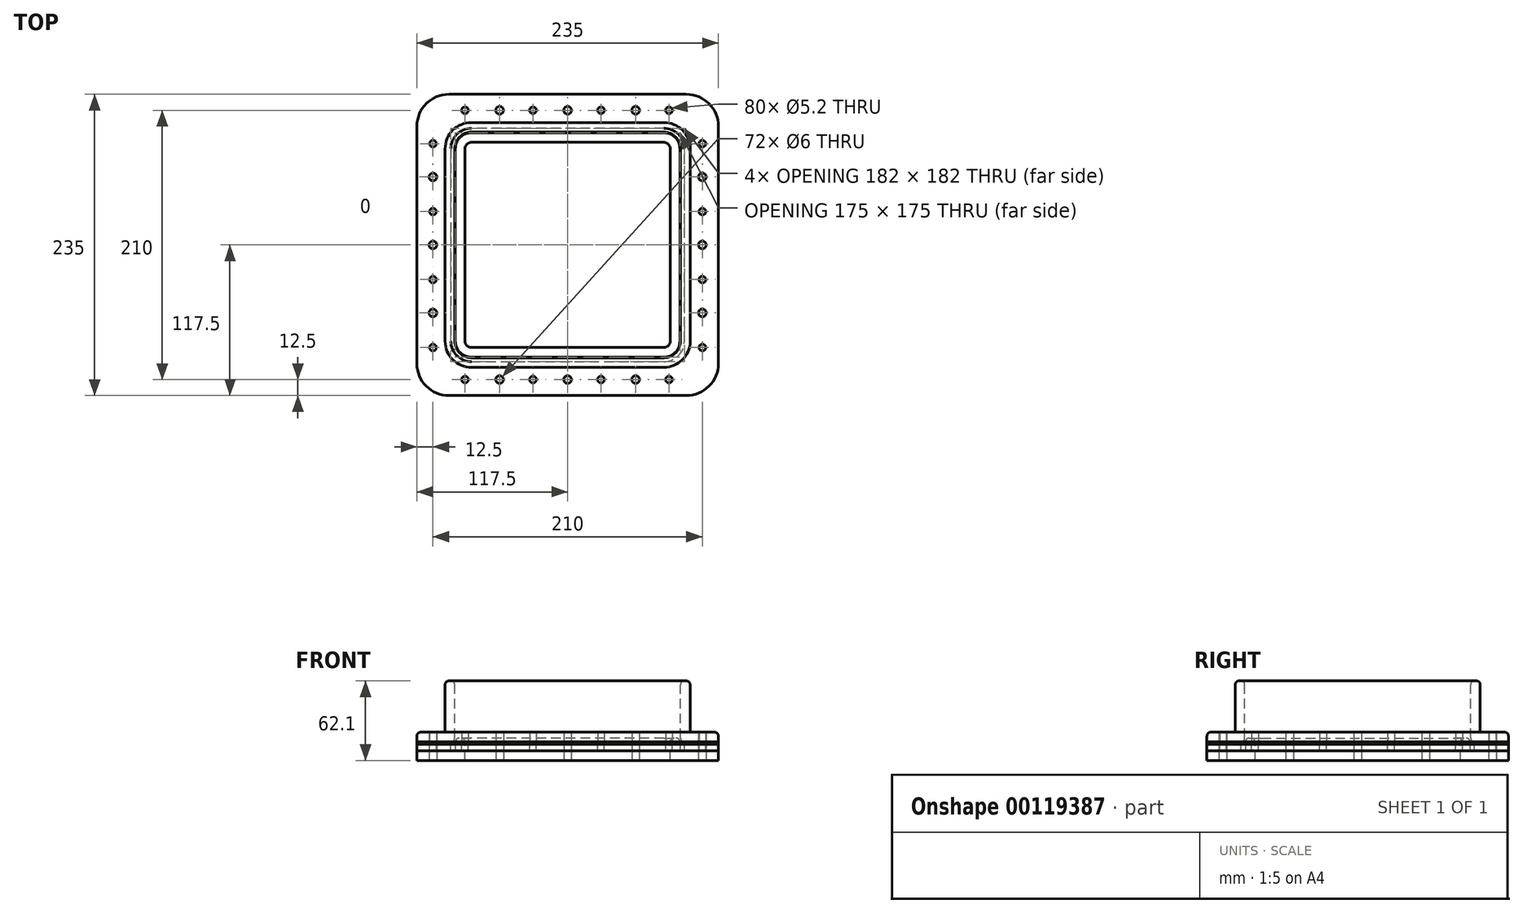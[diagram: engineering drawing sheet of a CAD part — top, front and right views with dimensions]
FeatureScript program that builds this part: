
annotation { "Feature Type Name" : "Feature", "Feature Type Description" : "" }
export const myFeature = defineFeature(function(context is Context, id is Id, definition is map)
    precondition{}
    {
        {
            var Q0;
            Q0=qCreatedBy(makeId("Top.planeOp"),FACE);
            var sketch = newSketch(context, id + "F0", { "sketchPlane" : qUnion([Q0])});
            skLineSegment(sketch, "E0.bottom", {"start": v(75, -80) * mm, "end": v(-75, -80) * mm});
            skLineSegment(sketch, "E0.top", {"start": v(75, 80) * mm, "end": v(-75, 80) * mm});
            skLineSegment(sketch, "E0.left", {"start": v(80, -75) * mm, "end": v(80, 75) * mm});
            skLineSegment(sketch, "E0.right", {"start": v(-80, -75) * mm, "end": v(-80, 75) * mm});
            skPoint(sketch, "E0.middle", {"position": v(0, 0) * mm});
            skLineSegment(sketch, "E1.bottom", {"start": v(75, -87.5) * mm, "end": v(-75, -87.5) * mm});
            skLineSegment(sketch, "E1.top", {"start": v(75, 87.5) * mm, "end": v(-75, 87.5) * mm});
            skLineSegment(sketch, "E1.left", {"start": v(87.5, -75) * mm, "end": v(87.5, 75) * mm});
            skLineSegment(sketch, "E1.right", {"start": v(-87.5, -75) * mm, "end": v(-87.5, 75) * mm});
            skLineSegment(sketch, "E2.bottom", {"start": v(92.5, -117.5) * mm, "end": v(-92.5, -117.5) * mm});
            skLineSegment(sketch, "E2.top", {"start": v(92.5, 117.5) * mm, "end": v(-92.5, 117.5) * mm});
            skLineSegment(sketch, "E2.left", {"start": v(117.5, -92.5) * mm, "end": v(117.5, 92.5) * mm});
            skLineSegment(sketch, "E2.right", {"start": v(-117.5, -92.5) * mm, "end": v(-117.5, 92.5) * mm});
            skPoint(sketch, "E3.visualSharp", {"position": v(-117.5, 117.5) * mm});
            skArc(sketch, "E3.filletArc", {"start": v(-92.5, 117.5) * mm, "mid": v(-110.18, 110.18) * mm, "end": v(-117.5, 92.5) * mm});
            skPoint(sketch, "E4.visualSharp", {"position": v(117.5, 117.5) * mm});
            skArc(sketch, "E4.filletArc", {"start": v(117.5, 92.5) * mm, "mid": v(110.18, 110.18) * mm, "end": v(92.5, 117.5) * mm});
            skPoint(sketch, "E5.visualSharp", {"position": v(117.5, -117.5) * mm});
            skArc(sketch, "E5.filletArc", {"start": v(92.5, -117.5) * mm, "mid": v(110.18, -110.18) * mm, "end": v(117.5, -92.5) * mm});
            skPoint(sketch, "E6.visualSharp", {"position": v(-117.5, -117.5) * mm});
            skArc(sketch, "E6.filletArc", {"start": v(-117.5, -92.5) * mm, "mid": v(-110.18, -110.18) * mm, "end": v(-92.5, -117.5) * mm});
            skPoint(sketch, "E7.visualSharp", {"position": v(-80, 80) * mm});
            skArc(sketch, "E7.filletArc", {"start": v(-75, 80) * mm, "mid": v(-78.54, 78.54) * mm, "end": v(-80, 75) * mm});
            skPoint(sketch, "E8.visualSharp", {"position": v(80, 80) * mm});
            skArc(sketch, "E8.filletArc", {"start": v(80, 75) * mm, "mid": v(78.54, 78.54) * mm, "end": v(75, 80) * mm});
            skPoint(sketch, "E9.visualSharp", {"position": v(80, -80) * mm});
            skArc(sketch, "E9.filletArc", {"start": v(75, -80) * mm, "mid": v(78.54, -78.54) * mm, "end": v(80, -75) * mm});
            skPoint(sketch, "E10.visualSharp", {"position": v(-80, -80) * mm});
            skArc(sketch, "E10.filletArc", {"start": v(-80, -75) * mm, "mid": v(-78.54, -78.54) * mm, "end": v(-75, -80) * mm});
            skPoint(sketch, "E11.visualSharp", {"position": v(-87.5, 87.5) * mm});
            skArc(sketch, "E11.filletArc", {"start": v(-75, 87.5) * mm, "mid": v(-83.84, 83.84) * mm, "end": v(-87.5, 75) * mm});
            skPoint(sketch, "E12.visualSharp", {"position": v(87.5, 87.5) * mm});
            skArc(sketch, "E12.filletArc", {"start": v(87.5, 75) * mm, "mid": v(83.84, 83.84) * mm, "end": v(75, 87.5) * mm});
            skPoint(sketch, "E13.visualSharp", {"position": v(87.5, -87.5) * mm});
            skArc(sketch, "E13.filletArc", {"start": v(75, -87.5) * mm, "mid": v(83.84, -83.84) * mm, "end": v(87.5, -75) * mm});
            skPoint(sketch, "E14.visualSharp", {"position": v(-87.5, -87.5) * mm});
            skArc(sketch, "E14.filletArc", {"start": v(-87.5, -75) * mm, "mid": v(-83.84, -83.84) * mm, "end": v(-75, -87.5) * mm});
            skSolve(sketch);
        }
        {
            var Q0;
            Q0=makeQuery(id+"F0.imprint","IMPRINT",FACE,{"disambiguationData":[TD([[makeQuery(id+"F0.imprint","IMPRINT",EDGE,{"derivedFrom":sQuery(id+"F0.wireOp",EDGE,"E0.bottom")}),1.0]])]});
            extrude(context, id + "F1", {"entities" : qUnion([Q0]), "depth" : 25 * mm});
        }
        {
            var Q0;
            Q0 = qSketchRegion(id + "F0", true);
            extrude(context, id + "F2", {"entities" : qUnion([Q0]), "operationType" : NewBodyOperationType.ADD, "depth" : 10 * mm});
        }
        {
            var Q0;
            Q0=makeQuery(id+"F1.opExtrude","CAP_FACE",FACE,{"disambiguationData":[OSD([sQuery(id+"F0.wireOp",EDGE,"E0.bottom"),sQuery(id+"F0.wireOp",EDGE,"E0.top"),sQuery(id+"F0.wireOp",EDGE,"E0.left"),sQuery(id+"F0.wireOp",EDGE,"E0.right"),sQuery(id+"F0.wireOp",EDGE,"E1.bottom"),sQuery(id+"F0.wireOp",EDGE,"E1.top"),sQuery(id+"F0.wireOp",EDGE,"E1.left"),sQuery(id+"F0.wireOp",EDGE,"E1.right"),sQuery(id+"F0.wireOp",EDGE,"E7.filletArc"),sQuery(id+"F0.wireOp",EDGE,"E8.filletArc"),sQuery(id+"F0.wireOp",EDGE,"E9.filletArc"),sQuery(id+"F0.wireOp",EDGE,"E10.filletArc"),sQuery(id+"F0.wireOp",EDGE,"E11.filletArc"),sQuery(id+"F0.wireOp",EDGE,"E12.filletArc"),sQuery(id+"F0.wireOp",EDGE,"E13.filletArc"),sQuery(id+"F0.wireOp",EDGE,"E14.filletArc")])],"isStart":false});
            fillet(context, id + "F3", {"entities" : qUnion([Q0]), "radius" : 3 * mm, "tangentPropagation" : true, "allowEdgeOverflow" : false});
        }
        {
            var Q0;
            Q0=makeQuery(id+"F2.opExtrude","CAP_FACE",FACE,{"disambiguationData":[OSD([sQuery(id+"F0.wireOp",EDGE,"E1.bottom"),sQuery(id+"F0.wireOp",EDGE,"E1.top"),sQuery(id+"F0.wireOp",EDGE,"E1.left"),sQuery(id+"F0.wireOp",EDGE,"E1.right"),sQuery(id+"F0.wireOp",EDGE,"E2.bottom"),sQuery(id+"F0.wireOp",EDGE,"E2.top"),sQuery(id+"F0.wireOp",EDGE,"E2.left"),sQuery(id+"F0.wireOp",EDGE,"E2.right"),sQuery(id+"F0.wireOp",EDGE,"E3.filletArc"),sQuery(id+"F0.wireOp",EDGE,"E4.filletArc"),sQuery(id+"F0.wireOp",EDGE,"E5.filletArc"),sQuery(id+"F0.wireOp",EDGE,"E6.filletArc"),sQuery(id+"F0.wireOp",EDGE,"E11.filletArc"),sQuery(id+"F0.wireOp",EDGE,"E12.filletArc"),sQuery(id+"F0.wireOp",EDGE,"E13.filletArc"),sQuery(id+"F0.wireOp",EDGE,"E14.filletArc")])],"isStart":false});
            extrude(context, id + "F4", {"entities" : qUnion([Q0]), "depth" : 7.5 * mm});
        }
        {
            var Q0;
            Q0=makeQuery(id+"F4.opExtrude","CAP_FACE",FACE,{"disambiguationData":[OSD([sQuery(id+"F0.wireOp",EDGE,"E1.bottom"),sQuery(id+"F0.wireOp",EDGE,"E1.top"),sQuery(id+"F0.wireOp",EDGE,"E1.left"),sQuery(id+"F0.wireOp",EDGE,"E1.right"),sQuery(id+"F0.wireOp",EDGE,"E2.bottom"),sQuery(id+"F0.wireOp",EDGE,"E2.top"),sQuery(id+"F0.wireOp",EDGE,"E2.left"),sQuery(id+"F0.wireOp",EDGE,"E2.right"),sQuery(id+"F0.wireOp",EDGE,"E3.filletArc"),sQuery(id+"F0.wireOp",EDGE,"E4.filletArc"),sQuery(id+"F0.wireOp",EDGE,"E5.filletArc"),sQuery(id+"F0.wireOp",EDGE,"E6.filletArc"),sQuery(id+"F0.wireOp",EDGE,"E11.filletArc"),sQuery(id+"F0.wireOp",EDGE,"E12.filletArc"),sQuery(id+"F0.wireOp",EDGE,"E13.filletArc"),sQuery(id+"F0.wireOp",EDGE,"E14.filletArc")])],"isStart":false});
            var sketch = newSketch(context, id + "F5", { "sketchPlane" : qUnion([Q0])});
            skLineSegment(sketch, "E15.bottom", {"start": v(75, -88) * mm, "end": v(-75, -88) * mm});
            skLineSegment(sketch, "E15.top", {"start": v(75, 88) * mm, "end": v(-75, 88) * mm});
            skLineSegment(sketch, "E15.left", {"start": v(88, -75) * mm, "end": v(88, 75) * mm});
            skLineSegment(sketch, "E15.right", {"start": v(-88, -75) * mm, "end": v(-88, 75) * mm});
            skPoint(sketch, "E15.middle", {"position": v(0, 0) * mm});
            skPoint(sketch, "E16.visualSharp", {"position": v(-88, 88) * mm});
            skArc(sketch, "E16.filletArc", {"start": v(-75, 88) * mm, "mid": v(-84.2, 84.2) * mm, "end": v(-88, 75) * mm});
            skPoint(sketch, "E17.visualSharp", {"position": v(88, 88) * mm});
            skArc(sketch, "E17.filletArc", {"start": v(88, 75) * mm, "mid": v(84.2, 84.2) * mm, "end": v(75, 88) * mm});
            skPoint(sketch, "E18.visualSharp", {"position": v(88, -88) * mm});
            skArc(sketch, "E18.filletArc", {"start": v(75, -88) * mm, "mid": v(84.2, -84.2) * mm, "end": v(88, -75) * mm});
            skPoint(sketch, "E19.visualSharp", {"position": v(-88, -88) * mm});
            skArc(sketch, "E19.filletArc", {"start": v(-88, -75) * mm, "mid": v(-84.2, -84.2) * mm, "end": v(-75, -88) * mm});
            skSolve(sketch);
        }
        {
            var Q0;
            Q0 = qSketchRegion(id + "F5", true);
            extrude(context, id + "F6", {"entities" : qUnion([Q0]), "operationType" : NewBodyOperationType.REMOVE, "oppositeDirection" : true, "depth" : 25 * mm});
        }
        {
            var Q0;
            Q0=makeQuery(id+"F4.opExtrude","CAP_FACE",FACE,{"disambiguationData":[OSD([sQuery(id+"F0.wireOp",EDGE,"E1.bottom"),sQuery(id+"F0.wireOp",EDGE,"E1.top"),sQuery(id+"F0.wireOp",EDGE,"E1.left"),sQuery(id+"F0.wireOp",EDGE,"E1.right"),sQuery(id+"F0.wireOp",EDGE,"E2.bottom"),sQuery(id+"F0.wireOp",EDGE,"E2.top"),sQuery(id+"F0.wireOp",EDGE,"E2.left"),sQuery(id+"F0.wireOp",EDGE,"E2.right"),sQuery(id+"F0.wireOp",EDGE,"E3.filletArc"),sQuery(id+"F0.wireOp",EDGE,"E4.filletArc"),sQuery(id+"F0.wireOp",EDGE,"E5.filletArc"),sQuery(id+"F0.wireOp",EDGE,"E6.filletArc"),sQuery(id+"F0.wireOp",EDGE,"E11.filletArc"),sQuery(id+"F0.wireOp",EDGE,"E12.filletArc"),sQuery(id+"F0.wireOp",EDGE,"E13.filletArc"),sQuery(id+"F0.wireOp",EDGE,"E14.filletArc")])],"isStart":false});
            var sketch = newSketch(context, id + "F7", { "sketchPlane" : qUnion([Q0])});
            skLineSegment(sketch, "E20.bottom", {"start": v(75, -88) * mm, "end": v(-75, -88) * mm});
            skLineSegment(sketch, "E20.top", {"start": v(75, 88) * mm, "end": v(-75, 88) * mm});
            skLineSegment(sketch, "E20.left", {"start": v(88, -75) * mm, "end": v(88, 75) * mm});
            skLineSegment(sketch, "E20.right", {"start": v(-88, -75) * mm, "end": v(-88, 75) * mm});
            skPoint(sketch, "E20.middle", {"position": v(0, 0) * mm});
            skPoint(sketch, "E21.visualSharp", {"position": v(-88, 88) * mm});
            skArc(sketch, "E21.filletArc", {"start": v(-75, 88) * mm, "mid": v(-84.2, 84.2) * mm, "end": v(-88, 75) * mm});
            skPoint(sketch, "E22.visualSharp", {"position": v(88, 88) * mm});
            skArc(sketch, "E22.filletArc", {"start": v(88, 75) * mm, "mid": v(84.2, 84.2) * mm, "end": v(75, 88) * mm});
            skPoint(sketch, "E23.visualSharp", {"position": v(88, -88) * mm});
            skArc(sketch, "E23.filletArc", {"start": v(75, -88) * mm, "mid": v(84.2, -84.2) * mm, "end": v(88, -75) * mm});
            skPoint(sketch, "E24.visualSharp", {"position": v(-88, -88) * mm});
            skArc(sketch, "E24.filletArc", {"start": v(-88, -75) * mm, "mid": v(-84.2, -84.2) * mm, "end": v(-75, -88) * mm});
            skLineSegment(sketch, "E25.bottom", {"start": v(75, -95.5) * mm, "end": v(-75, -95.5) * mm});
            skLineSegment(sketch, "E25.top", {"start": v(75, 95.5) * mm, "end": v(-75, 95.5) * mm});
            skLineSegment(sketch, "E25.left", {"start": v(95.5, -75) * mm, "end": v(95.5, 75) * mm});
            skLineSegment(sketch, "E25.right", {"start": v(-95.5, -75) * mm, "end": v(-95.5, 75) * mm});
            skPoint(sketch, "E26.visualSharp", {"position": v(-95.5, 95.5) * mm});
            skArc(sketch, "E26.filletArc", {"start": v(-75, 95.5) * mm, "mid": v(-89.5, 89.5) * mm, "end": v(-95.5, 75) * mm});
            skPoint(sketch, "E27.visualSharp", {"position": v(95.5, 95.5) * mm});
            skArc(sketch, "E27.filletArc", {"start": v(95.5, 75) * mm, "mid": v(89.5, 89.5) * mm, "end": v(75, 95.5) * mm});
            skPoint(sketch, "E28.visualSharp", {"position": v(95.5, -95.5) * mm});
            skArc(sketch, "E28.filletArc", {"start": v(75, -95.5) * mm, "mid": v(89.5, -89.5) * mm, "end": v(95.5, -75) * mm});
            skPoint(sketch, "E29.visualSharp", {"position": v(-95.5, -95.5) * mm});
            skArc(sketch, "E29.filletArc", {"start": v(-95.5, -75) * mm, "mid": v(-89.5, -89.5) * mm, "end": v(-75, -95.5) * mm});
            skSolve(sketch);
        }
        {
            var Q0;
            Q0=makeQuery(id+"F7.imprint","IMPRINT",FACE,{"disambiguationData":[TD([[makeQuery(id+"F7.imprint","IMPRINT",EDGE,{"derivedFrom":sQuery(id+"F7.wireOp",EDGE,"E20.bottom")}),1.0]])]});
            extrude(context, id + "F8", {"entities" : qUnion([Q0]), "operationType" : NewBodyOperationType.ADD, "depth" : 40 * mm});
        }
        {
            var Q0;
            Q0=makeQuery(id+"F8.opExtrude","CAP_FACE",FACE,{"disambiguationData":[OSD([sQuery(id+"F7.wireOp",EDGE,"E20.bottom"),sQuery(id+"F7.wireOp",EDGE,"E20.top"),sQuery(id+"F7.wireOp",EDGE,"E20.left"),sQuery(id+"F7.wireOp",EDGE,"E20.right"),sQuery(id+"F7.wireOp",EDGE,"E21.filletArc"),sQuery(id+"F7.wireOp",EDGE,"E22.filletArc"),sQuery(id+"F7.wireOp",EDGE,"E23.filletArc"),sQuery(id+"F7.wireOp",EDGE,"E24.filletArc"),sQuery(id+"F7.wireOp",EDGE,"E25.bottom"),sQuery(id+"F7.wireOp",EDGE,"E25.top"),sQuery(id+"F7.wireOp",EDGE,"E25.left"),sQuery(id+"F7.wireOp",EDGE,"E25.right"),sQuery(id+"F7.wireOp",EDGE,"E26.filletArc"),sQuery(id+"F7.wireOp",EDGE,"E27.filletArc"),sQuery(id+"F7.wireOp",EDGE,"E28.filletArc"),sQuery(id+"F7.wireOp",EDGE,"E29.filletArc")])],"isStart":false});
            var Q1;
            Q1=makeQuery(id+"F4.opExtrude","CAP_EDGE",EDGE,{"disambiguationData":[OSD([sQuery(id+"F0.wireOp",EDGE,"E2.top")])],"isStart":false});
            fillet(context, id + "F9", {"entities" : qUnion([Q0, Q1]), "radius" : 3 * mm, "tangentPropagation" : true, "allowEdgeOverflow" : false});
        }
        {
            var Q0;
            Q0=makeQuery(id+"F6.boolean.opBoolean","INTERSECT",EDGE,{"derivedFrom":[makeQuery(id+"F4.opExtrude","CAP_FACE",FACE,{"disambiguationData":[OSD([sQuery(id+"F0.wireOp",EDGE,"E1.bottom"),sQuery(id+"F0.wireOp",EDGE,"E1.top"),sQuery(id+"F0.wireOp",EDGE,"E1.left"),sQuery(id+"F0.wireOp",EDGE,"E1.right"),sQuery(id+"F0.wireOp",EDGE,"E2.bottom"),sQuery(id+"F0.wireOp",EDGE,"E2.top"),sQuery(id+"F0.wireOp",EDGE,"E2.left"),sQuery(id+"F0.wireOp",EDGE,"E2.right"),sQuery(id+"F0.wireOp",EDGE,"E3.filletArc"),sQuery(id+"F0.wireOp",EDGE,"E4.filletArc"),sQuery(id+"F0.wireOp",EDGE,"E5.filletArc"),sQuery(id+"F0.wireOp",EDGE,"E6.filletArc"),sQuery(id+"F0.wireOp",EDGE,"E11.filletArc"),sQuery(id+"F0.wireOp",EDGE,"E12.filletArc"),sQuery(id+"F0.wireOp",EDGE,"E13.filletArc"),sQuery(id+"F0.wireOp",EDGE,"E14.filletArc")])],"isStart":true}),makeQuery(id+"F6.opExtrude","SWEPT_FACE",FACE,{"disambiguationData":[OSD([sQuery(id+"F5.wireOp",EDGE,"E15.bottom")])]})]});
            fillet(context, id + "F10", {"entities" : qUnion([Q0]), "radius" : 3 * mm, "tangentPropagation" : true, "allowEdgeOverflow" : false});
        }
        {
            var Q0;
            {var subQ0=sQuery(id+"F0.wireOp",EDGE,"E14.filletArc");var subQ1=sQuery(id+"F0.wireOp",EDGE,"E13.filletArc");var subQ2=sQuery(id+"F0.wireOp",EDGE,"E12.filletArc");var subQ3=sQuery(id+"F0.wireOp",EDGE,"E11.filletArc");var subQ4=sQuery(id+"F0.wireOp",EDGE,"E1.right");var subQ5=sQuery(id+"F0.wireOp",EDGE,"E1.left");var subQ6=sQuery(id+"F0.wireOp",EDGE,"E1.top");var subQ7=sQuery(id+"F0.wireOp",EDGE,"E1.bottom");Q0=makeQuery(id+"F2.boolean.opBoolean","MERGE",FACE,{"derivedFrom":[makeQuery(id+"F1.opExtrude","CAP_FACE",FACE,{"disambiguationData":[OSD([sQuery(id+"F0.wireOp",EDGE,"E0.bottom"),sQuery(id+"F0.wireOp",EDGE,"E0.top"),sQuery(id+"F0.wireOp",EDGE,"E0.left"),sQuery(id+"F0.wireOp",EDGE,"E0.right"),subQ7,subQ6,subQ5,subQ4,sQuery(id+"F0.wireOp",EDGE,"E7.filletArc"),sQuery(id+"F0.wireOp",EDGE,"E8.filletArc"),sQuery(id+"F0.wireOp",EDGE,"E9.filletArc"),sQuery(id+"F0.wireOp",EDGE,"E10.filletArc"),subQ3,subQ2,subQ1,subQ0])],"isStart":true}),makeQuery(id+"F2.opExtrude","CAP_FACE",FACE,{"disambiguationData":[OSD([subQ7,subQ6,subQ5,subQ4,sQuery(id+"F0.wireOp",EDGE,"E2.bottom"),sQuery(id+"F0.wireOp",EDGE,"E2.top"),sQuery(id+"F0.wireOp",EDGE,"E2.left"),sQuery(id+"F0.wireOp",EDGE,"E2.right"),sQuery(id+"F0.wireOp",EDGE,"E3.filletArc"),sQuery(id+"F0.wireOp",EDGE,"E4.filletArc"),sQuery(id+"F0.wireOp",EDGE,"E5.filletArc"),sQuery(id+"F0.wireOp",EDGE,"E6.filletArc"),subQ3,subQ2,subQ1,subQ0])],"isStart":true})]});}
            var sketch = newSketch(context, id + "F11", { "sketchPlane" : qUnion([Q0])});
            skLineSegment(sketch, "E30.bottom", {"start": v(105, -105) * mm, "end": v(-105, -105) * mm, "construction": true});
            skLineSegment(sketch, "E30.top", {"start": v(105, 105) * mm, "end": v(-105, 105) * mm, "construction": true});
            skLineSegment(sketch, "E30.left", {"start": v(105, -105) * mm, "end": v(105, 105) * mm, "construction": true});
            skLineSegment(sketch, "E30.right", {"start": v(-105, -105) * mm, "end": v(-105, 105) * mm, "construction": true});
            skPoint(sketch, "E30.middle", {"position": v(0, 0) * mm});
            skLineSegment(sketch, "E31", {"start": v(-80, 0) * mm, "end": v(-80, 124.18) * mm, "construction": true});
            skLineSegment(sketch, "E32", {"start": v(0, 80) * mm, "end": v(-105, 80) * mm, "construction": true});
            skCircle(sketch, "E33", {"center": v(-80, 105) * mm, "radius": 2.6 * mm});
            skCircle(sketch, "E34", {"center": v(-105, 80) * mm, "radius": 2.6 * mm});
            skCircle(sketch, "E35.0.1.0", {"center": v(-80, -105) * mm, "radius": 2.6 * mm});
            skCircle(sketch, "E35.1.0.0", {"center": v(-27, 105) * mm, "radius": 2.6 * mm});
            skCircle(sketch, "E35.1.1.0", {"center": v(-27, -105) * mm, "radius": 2.6 * mm});
            skCircle(sketch, "E35.2.0.0", {"center": v(26, 105) * mm, "radius": 2.6 * mm});
            skCircle(sketch, "E35.2.1.0", {"center": v(26, -105) * mm, "radius": 2.6 * mm});
            skCircle(sketch, "E35.3.0.0", {"center": v(79, 105) * mm, "radius": 2.6 * mm});
            skCircle(sketch, "E35.3.1.0", {"center": v(79, -105) * mm, "radius": 2.6 * mm});
            skLineSegment(sketch, "E35.direction1", {"start": v(-80, 105) * mm, "end": v(-27, 105) * mm, "construction": true});
            skLineSegment(sketch, "E35.direction2", {"start": v(-80, 105) * mm, "end": v(-80, -105) * mm, "construction": true});
            skCircle(sketch, "E36.0.1.0", {"center": v(-105, 27) * mm, "radius": 2.6 * mm});
            skCircle(sketch, "E36.0.2.0", {"center": v(-105, -26) * mm, "radius": 2.6 * mm});
            skCircle(sketch, "E36.0.3.0", {"center": v(-105, -79) * mm, "radius": 2.6 * mm});
            skCircle(sketch, "E36.1.0.0", {"center": v(105, 80) * mm, "radius": 2.6 * mm});
            skCircle(sketch, "E36.1.1.0", {"center": v(105, 27) * mm, "radius": 2.6 * mm});
            skCircle(sketch, "E36.1.2.0", {"center": v(105, -26) * mm, "radius": 2.6 * mm});
            skCircle(sketch, "E36.1.3.0", {"center": v(105, -79) * mm, "radius": 2.6 * mm});
            skLineSegment(sketch, "E36.direction1", {"start": v(-105, 80) * mm, "end": v(105, 80) * mm, "construction": true});
            skLineSegment(sketch, "E36.direction2", {"start": v(-105, 80) * mm, "end": v(-105, 27) * mm, "construction": true});
            skSolve(sketch);
        }
        {
            var Q0;
            Q0=makeQuery(id+"F1.opExtrude","SWEPT_BODY",BODY,{"disambiguationData":[OSD([sQuery(id+"F0.wireOp",EDGE,"E0.bottom"),sQuery(id+"F0.wireOp",EDGE,"E0.top"),sQuery(id+"F0.wireOp",EDGE,"E0.left"),sQuery(id+"F0.wireOp",EDGE,"E0.right"),sQuery(id+"F0.wireOp",EDGE,"E1.bottom"),sQuery(id+"F0.wireOp",EDGE,"E1.top"),sQuery(id+"F0.wireOp",EDGE,"E1.left"),sQuery(id+"F0.wireOp",EDGE,"E1.right"),sQuery(id+"F0.wireOp",EDGE,"E7.filletArc"),sQuery(id+"F0.wireOp",EDGE,"E8.filletArc"),sQuery(id+"F0.wireOp",EDGE,"E9.filletArc"),sQuery(id+"F0.wireOp",EDGE,"E10.filletArc"),sQuery(id+"F0.wireOp",EDGE,"E11.filletArc"),sQuery(id+"F0.wireOp",EDGE,"E12.filletArc"),sQuery(id+"F0.wireOp",EDGE,"E13.filletArc"),sQuery(id+"F0.wireOp",EDGE,"E14.filletArc")])]});
            deleteBodies(context, id + "F12", {"entities" : qUnion([Q0])});
        }
        {
            var Q0;
            Q0 = qSketchRegion(id + "F11", true);
            extrude(context, id + "F13", {"entities" : qUnion([Q0]), "operationType" : NewBodyOperationType.REMOVE, "oppositeDirection" : true, "depth" : 25 * mm});
        }
        {
            var Q0;
            Q0=makeQuery(id+"F4.opExtrude","CAP_FACE",FACE,{"disambiguationData":[OSD([sQuery(id+"F0.wireOp",EDGE,"E1.bottom"),sQuery(id+"F0.wireOp",EDGE,"E1.top"),sQuery(id+"F0.wireOp",EDGE,"E1.left"),sQuery(id+"F0.wireOp",EDGE,"E1.right"),sQuery(id+"F0.wireOp",EDGE,"E2.bottom"),sQuery(id+"F0.wireOp",EDGE,"E2.top"),sQuery(id+"F0.wireOp",EDGE,"E2.left"),sQuery(id+"F0.wireOp",EDGE,"E2.right"),sQuery(id+"F0.wireOp",EDGE,"E3.filletArc"),sQuery(id+"F0.wireOp",EDGE,"E4.filletArc"),sQuery(id+"F0.wireOp",EDGE,"E5.filletArc"),sQuery(id+"F0.wireOp",EDGE,"E6.filletArc"),sQuery(id+"F0.wireOp",EDGE,"E11.filletArc"),sQuery(id+"F0.wireOp",EDGE,"E12.filletArc"),sQuery(id+"F0.wireOp",EDGE,"E13.filletArc"),sQuery(id+"F0.wireOp",EDGE,"E14.filletArc")])],"isStart":true});
            var sketch = newSketch(context, id + "F14", { "sketchPlane" : qUnion([Q0])});
            skLineSegment(sketch, "E37.bottom", {"start": v(75, -91) * mm, "end": v(-75, -91) * mm});
            skLineSegment(sketch, "E37.top", {"start": v(75, 91) * mm, "end": v(-75, 91) * mm});
            skLineSegment(sketch, "E37.left", {"start": v(91, -75) * mm, "end": v(91, 75) * mm});
            skLineSegment(sketch, "E37.right", {"start": v(-91, -75) * mm, "end": v(-91, 75) * mm});
            skPoint(sketch, "E37.middle", {"position": v(0, 0) * mm});
            skPoint(sketch, "E37.cornerSnap0", {"position": v(91, 0) * mm});
            skPoint(sketch, "E38.visualSharp", {"position": v(-91, 91) * mm});
            skArc(sketch, "E38.filletArc", {"start": v(-75, 91) * mm, "mid": v(-86.31, 86.31) * mm, "end": v(-91, 75) * mm});
            skPoint(sketch, "E39.visualSharp", {"position": v(91, 91) * mm});
            skArc(sketch, "E39.filletArc", {"start": v(91, 75) * mm, "mid": v(86.31, 86.31) * mm, "end": v(75, 91) * mm});
            skPoint(sketch, "E40.visualSharp", {"position": v(91, -91) * mm});
            skArc(sketch, "E40.filletArc", {"start": v(75, -91) * mm, "mid": v(86.31, -86.31) * mm, "end": v(91, -75) * mm});
            skPoint(sketch, "E41.visualSharp", {"position": v(-91, -91) * mm});
            skArc(sketch, "E41.filletArc", {"start": v(-91, -75) * mm, "mid": v(-86.31, -86.31) * mm, "end": v(-75, -91) * mm});
            skCircle(sketch, "E42", {"center": v(79, 105) * mm, "radius": 2.6 * mm});
            skCircle(sketch, "E43", {"center": v(79, -105) * mm, "radius": 2.6 * mm});
            skCircle(sketch, "E44", {"center": v(-105, 27) * mm, "radius": 2.6 * mm});
            skCircle(sketch, "E45", {"center": v(-80, -105) * mm, "radius": 2.6 * mm});
            skCircle(sketch, "E46", {"center": v(-27, 105) * mm, "radius": 2.6 * mm});
            skCircle(sketch, "E47", {"center": v(-27, -105) * mm, "radius": 2.6 * mm});
            skCircle(sketch, "E48", {"center": v(26, 105) * mm, "radius": 2.6 * mm});
            skCircle(sketch, "E49", {"center": v(-80, 105) * mm, "radius": 2.6 * mm});
            skCircle(sketch, "E50", {"center": v(105, -79) * mm, "radius": 2.6 * mm});
            skCircle(sketch, "E51", {"center": v(105, -26) * mm, "radius": 2.6 * mm});
            skCircle(sketch, "E52", {"center": v(105, 27) * mm, "radius": 2.6 * mm});
            skCircle(sketch, "E53", {"center": v(105, 80) * mm, "radius": 2.6 * mm});
            skCircle(sketch, "E54", {"center": v(-105, -79) * mm, "radius": 2.6 * mm});
            skCircle(sketch, "E55", {"center": v(-105, -26) * mm, "radius": 2.6 * mm});
            skCircle(sketch, "E56", {"center": v(-105, 80) * mm, "radius": 2.6 * mm});
            skArc(sketch, "E57", {"start": v(91, -75) * mm, "mid": v(86.31, -86.31) * mm, "end": v(75, -91) * mm});
            skLineSegment(sketch, "E58", {"start": v(91, 75) * mm, "end": v(91, -75) * mm});
            skArc(sketch, "E59", {"start": v(75, 91) * mm, "mid": v(86.31, 86.31) * mm, "end": v(91, 75) * mm});
            skLineSegment(sketch, "E60", {"start": v(-75, 91) * mm, "end": v(75, 91) * mm});
            skArc(sketch, "E61", {"start": v(-91, 75) * mm, "mid": v(-86.31, 86.31) * mm, "end": v(-75, 91) * mm});
            skArc(sketch, "E62", {"start": v(-75, -91) * mm, "mid": v(-86.31, -86.31) * mm, "end": v(-91, -75) * mm});
            skLineSegment(sketch, "E63", {"start": v(92.5, 117.5) * mm, "end": v(-92.5, 117.5) * mm});
            skArc(sketch, "E64", {"start": v(92.5, 117.5) * mm, "mid": v(110.18, 110.18) * mm, "end": v(117.5, 92.5) * mm});
            skLineSegment(sketch, "E65", {"start": v(117.5, 92.5) * mm, "end": v(117.5, -92.5) * mm});
            skArc(sketch, "E66", {"start": v(117.5, -92.5) * mm, "mid": v(110.18, -110.18) * mm, "end": v(92.5, -117.5) * mm});
            skLineSegment(sketch, "E67", {"start": v(92.5, -117.5) * mm, "end": v(-92.5, -117.5) * mm});
            skArc(sketch, "E68", {"start": v(-92.5, -117.5) * mm, "mid": v(-110.18, -110.18) * mm, "end": v(-117.5, -92.5) * mm});
            skLineSegment(sketch, "E69", {"start": v(-117.5, 92.5) * mm, "end": v(-117.5, -92.5) * mm});
            skArc(sketch, "E70", {"start": v(-117.5, 92.5) * mm, "mid": v(-110.18, 110.18) * mm, "end": v(-92.5, 117.5) * mm});
            skCircle(sketch, "E71", {"center": v(26, -105) * mm, "radius": 2.6 * mm});
            skSolve(sketch);
        }
        {
            var Q0;
            Q0 = qSketchRegion(id + "F14", true);
            extrude(context, id + "F15", {"entities" : qUnion([Q0]), "depth" : 1 * mm});
        }
        {
            var Q0;
            Q0=makeQuery(id+"F15.opExtrude","CAP_FACE",FACE,{"disambiguationData":[OSD([sQuery(id+"F14.wireOp",EDGE,"E42"),sQuery(id+"F14.wireOp",EDGE,"E43"),sQuery(id+"F14.wireOp",EDGE,"E44"),sQuery(id+"F14.wireOp",EDGE,"E45"),sQuery(id+"F14.wireOp",EDGE,"E46"),sQuery(id+"F14.wireOp",EDGE,"E47"),sQuery(id+"F14.wireOp",EDGE,"E48"),sQuery(id+"F14.wireOp",EDGE,"E49"),sQuery(id+"F14.wireOp",EDGE,"E50"),sQuery(id+"F14.wireOp",EDGE,"E51"),sQuery(id+"F14.wireOp",EDGE,"E52"),sQuery(id+"F14.wireOp",EDGE,"E53"),sQuery(id+"F14.wireOp",EDGE,"E54"),sQuery(id+"F14.wireOp",EDGE,"E55"),sQuery(id+"F14.wireOp",EDGE,"E56"),sQuery(id+"F14.wireOp",EDGE,"E57"),sQuery(id+"F14.wireOp",EDGE,"E58"),sQuery(id+"F14.wireOp",EDGE,"E59"),sQuery(id+"F14.wireOp",EDGE,"E60"),sQuery(id+"F14.wireOp",EDGE,"E61"),sQuery(id+"F14.wireOp",EDGE,"E37.right"),sQuery(id+"F14.wireOp",EDGE,"E62"),sQuery(id+"F14.wireOp",EDGE,"E37.bottom"),sQuery(id+"F14.wireOp",EDGE,"E63"),sQuery(id+"F14.wireOp",EDGE,"E64"),sQuery(id+"F14.wireOp",EDGE,"E65"),sQuery(id+"F14.wireOp",EDGE,"E66"),sQuery(id+"F14.wireOp",EDGE,"E67"),sQuery(id+"F14.wireOp",EDGE,"E68"),sQuery(id+"F14.wireOp",EDGE,"E69"),sQuery(id+"F14.wireOp",EDGE,"E70"),sQuery(id+"F14.wireOp",EDGE,"E71")])],"isStart":false});
            var sketch = newSketch(context, id + "F16", { "sketchPlane" : qUnion([Q0])});
            skCircle(sketch, "E72", {"center": v(79, 105) * mm, "radius": 2.6 * mm});
            skCircle(sketch, "E73", {"center": v(79, -105) * mm, "radius": 2.6 * mm});
            skCircle(sketch, "E74", {"center": v(-105, 27) * mm, "radius": 2.6 * mm});
            skCircle(sketch, "E75", {"center": v(-80, -105) * mm, "radius": 2.6 * mm});
            skCircle(sketch, "E76", {"center": v(-27, 105) * mm, "radius": 2.6 * mm});
            skCircle(sketch, "E77", {"center": v(-27, -105) * mm, "radius": 2.6 * mm});
            skCircle(sketch, "E78", {"center": v(26, 105) * mm, "radius": 2.6 * mm});
            skCircle(sketch, "E79", {"center": v(-80, 105) * mm, "radius": 2.6 * mm});
            skCircle(sketch, "E80", {"center": v(105, -79) * mm, "radius": 2.6 * mm});
            skCircle(sketch, "E81", {"center": v(105, -26) * mm, "radius": 2.6 * mm});
            skCircle(sketch, "E82", {"center": v(105, 27) * mm, "radius": 2.6 * mm});
            skCircle(sketch, "E83", {"center": v(105, 80) * mm, "radius": 2.6 * mm});
            skCircle(sketch, "E84", {"center": v(-105, -79) * mm, "radius": 2.6 * mm});
            skCircle(sketch, "E85", {"center": v(-105, -26) * mm, "radius": 2.6 * mm});
            skCircle(sketch, "E86", {"center": v(-105, 80) * mm, "radius": 2.6 * mm});
            skLineSegment(sketch, "E87", {"start": v(92.5, 117.5) * mm, "end": v(-92.5, 117.5) * mm});
            skArc(sketch, "E88", {"start": v(92.5, 117.5) * mm, "mid": v(110.18, 110.18) * mm, "end": v(117.5, 92.5) * mm});
            skLineSegment(sketch, "E89", {"start": v(117.5, 92.5) * mm, "end": v(117.5, -92.5) * mm});
            skArc(sketch, "E90", {"start": v(117.5, -92.5) * mm, "mid": v(110.18, -110.18) * mm, "end": v(92.5, -117.5) * mm});
            skLineSegment(sketch, "E91", {"start": v(92.5, -117.5) * mm, "end": v(-92.5, -117.5) * mm});
            skArc(sketch, "E92", {"start": v(-92.5, -117.5) * mm, "mid": v(-110.18, -110.18) * mm, "end": v(-117.5, -92.5) * mm});
            skLineSegment(sketch, "E93", {"start": v(-117.5, 92.5) * mm, "end": v(-117.5, -92.5) * mm});
            skArc(sketch, "E94", {"start": v(-117.5, 92.5) * mm, "mid": v(-110.18, 110.18) * mm, "end": v(-92.5, 117.5) * mm});
            skCircle(sketch, "E95", {"center": v(26, -105) * mm, "radius": 2.6 * mm});
            skSolve(sketch);
        }
        {
            var Q0;
            Q0 = qSketchRegion(id + "F16", true);
            var Q1;
            Q1=makeQuery(id+"F16.imprint","IMPRINT",FACE,{"disambiguationData":[TD([[makeQuery(id+"F16.imprint","IMPRINT",EDGE,{"derivedFrom":sQuery(id+"F16.wireOp",EDGE,"E743")}),-1.0]])]});
            extrude(context, id + "F17", {"entities" : qUnion([Q0, Q1]), "depth" : .1 * mm});
        }
        {
            var Q0;
            Q0=makeQuery(id+"F17.opExtrude","CAP_FACE",FACE,{"disambiguationData":[OSD([sQuery(id+"F16.wireOp",EDGE,"E72"),sQuery(id+"F16.wireOp",EDGE,"E73"),sQuery(id+"F16.wireOp",EDGE,"E74"),sQuery(id+"F16.wireOp",EDGE,"E75"),sQuery(id+"F16.wireOp",EDGE,"E76"),sQuery(id+"F16.wireOp",EDGE,"E77"),sQuery(id+"F16.wireOp",EDGE,"E78"),sQuery(id+"F16.wireOp",EDGE,"E79"),sQuery(id+"F16.wireOp",EDGE,"E80"),sQuery(id+"F16.wireOp",EDGE,"E81"),sQuery(id+"F16.wireOp",EDGE,"E82"),sQuery(id+"F16.wireOp",EDGE,"E83"),sQuery(id+"F16.wireOp",EDGE,"E84"),sQuery(id+"F16.wireOp",EDGE,"E85"),sQuery(id+"F16.wireOp",EDGE,"E86"),sQuery(id+"F16.wireOp",EDGE,"E87"),sQuery(id+"F16.wireOp",EDGE,"E88"),sQuery(id+"F16.wireOp",EDGE,"E89"),sQuery(id+"F16.wireOp",EDGE,"E90"),sQuery(id+"F16.wireOp",EDGE,"E91"),sQuery(id+"F16.wireOp",EDGE,"E92"),sQuery(id+"F16.wireOp",EDGE,"E93"),sQuery(id+"F16.wireOp",EDGE,"E94"),sQuery(id+"F16.wireOp",EDGE,"E95")])],"isStart":false});
            var sketch = newSketch(context, id + "F18", { "sketchPlane" : qUnion([Q0])});
            skCircle(sketch, "E96", {"center": v(-105, 27) * mm, "radius": 2.6 * mm});
            skCircle(sketch, "E97", {"center": v(-27, 105) * mm, "radius": 2.6 * mm});
            skCircle(sketch, "E98", {"center": v(26, 105) * mm, "radius": 2.6 * mm});
            skCircle(sketch, "E99", {"center": v(105, -79) * mm, "radius": 2.6 * mm});
            skCircle(sketch, "E100", {"center": v(105, 27) * mm, "radius": 2.6 * mm});
            skCircle(sketch, "E101", {"center": v(-105, -79) * mm, "radius": 2.6 * mm});
            skLineSegment(sketch, "E102", {"start": v(92.5, 117.5) * mm, "end": v(-92.5, 117.5) * mm});
            skArc(sketch, "E103", {"start": v(92.5, 117.5) * mm, "mid": v(110.18, 110.18) * mm, "end": v(117.5, 92.5) * mm});
            skLineSegment(sketch, "E104", {"start": v(117.5, 92.5) * mm, "end": v(117.5, -92.5) * mm});
            skArc(sketch, "E105", {"start": v(117.5, -92.5) * mm, "mid": v(110.18, -110.18) * mm, "end": v(92.5, -117.5) * mm});
            skLineSegment(sketch, "E106", {"start": v(92.5, -117.5) * mm, "end": v(-92.5, -117.5) * mm});
            skArc(sketch, "E107", {"start": v(-92.5, -117.5) * mm, "mid": v(-110.18, -110.18) * mm, "end": v(-117.5, -92.5) * mm});
            skLineSegment(sketch, "E108", {"start": v(-117.5, 92.5) * mm, "end": v(-117.5, -92.5) * mm});
            skArc(sketch, "E109", {"start": v(-117.5, 92.5) * mm, "mid": v(-110.18, 110.18) * mm, "end": v(-92.5, 117.5) * mm});
            skCircle(sketch, "E110", {"center": v(-105, 80) * mm, "radius": 2.6 * mm});
            skCircle(sketch, "E111", {"center": v(-105, -26) * mm, "radius": 2.6 * mm});
            skCircle(sketch, "E112", {"center": v(105, 80) * mm, "radius": 2.6 * mm});
            skCircle(sketch, "E113", {"center": v(105, -26) * mm, "radius": 2.6 * mm});
            skCircle(sketch, "E114", {"center": v(-80, 105) * mm, "radius": 2.6 * mm});
            skCircle(sketch, "E115", {"center": v(-27, -105) * mm, "radius": 2.6 * mm});
            skCircle(sketch, "E116", {"center": v(-80, -105) * mm, "radius": 2.6 * mm});
            skCircle(sketch, "E117", {"center": v(79, -105) * mm, "radius": 2.6 * mm});
            skCircle(sketch, "E118", {"center": v(26, -105) * mm, "radius": 2.6 * mm});
            skCircle(sketch, "E119", {"center": v(79, 105) * mm, "radius": 2.6 * mm});
            skLineSegment(sketch, "E120.0", {"start": v(-75, 91) * mm, "end": v(75, 91) * mm});
            skArc(sketch, "E120.1", {"start": v(75, 91) * mm, "mid": v(86.31, 86.31) * mm, "end": v(91, 75) * mm});
            skLineSegment(sketch, "E120.2", {"start": v(91, 75) * mm, "end": v(91, -75) * mm});
            skArc(sketch, "E120.3", {"start": v(91, -75) * mm, "mid": v(86.31, -86.31) * mm, "end": v(75, -91) * mm});
            skLineSegment(sketch, "E120.4", {"start": v(75, -91) * mm, "end": v(-75, -91) * mm});
            skArc(sketch, "E120.5", {"start": v(-75, -91) * mm, "mid": v(-86.31, -86.31) * mm, "end": v(-91, -75) * mm});
            skLineSegment(sketch, "E120.6", {"start": v(-91, -75) * mm, "end": v(-91, 75) * mm});
            skArc(sketch, "E120.7", {"start": v(-91, 75) * mm, "mid": v(-86.31, 86.31) * mm, "end": v(-75, 91) * mm});
            skSolve(sketch);
        }
        {
            var Q0;
            Q0 = qSketchRegion(id + "F18", true);
            extrude(context, id + "F19", {"entities" : qUnion([Q0]), "depth" : 1 * mm});
        }
        {
            var Q0;
            Q0=makeQuery(id+"F19.opExtrude","CAP_FACE",FACE,{"disambiguationData":[OSD([sQuery(id+"F18.wireOp",EDGE,"E96"),sQuery(id+"F18.wireOp",EDGE,"E97"),sQuery(id+"F18.wireOp",EDGE,"E98"),sQuery(id+"F18.wireOp",EDGE,"E99"),sQuery(id+"F18.wireOp",EDGE,"E100"),sQuery(id+"F18.wireOp",EDGE,"E101"),sQuery(id+"F18.wireOp",EDGE,"E102"),sQuery(id+"F18.wireOp",EDGE,"E103"),sQuery(id+"F18.wireOp",EDGE,"E104"),sQuery(id+"F18.wireOp",EDGE,"E105"),sQuery(id+"F18.wireOp",EDGE,"E106"),sQuery(id+"F18.wireOp",EDGE,"E107"),sQuery(id+"F18.wireOp",EDGE,"E108"),sQuery(id+"F18.wireOp",EDGE,"E109"),sQuery(id+"F18.wireOp",EDGE,"E110"),sQuery(id+"F18.wireOp",EDGE,"E111"),sQuery(id+"F18.wireOp",EDGE,"E112"),sQuery(id+"F18.wireOp",EDGE,"E113"),sQuery(id+"F18.wireOp",EDGE,"E114"),sQuery(id+"F18.wireOp",EDGE,"E115"),sQuery(id+"F18.wireOp",EDGE,"E116"),sQuery(id+"F18.wireOp",EDGE,"E117"),sQuery(id+"F18.wireOp",EDGE,"E118"),sQuery(id+"F18.wireOp",EDGE,"E119"),sQuery(id+"F18.wireOp",EDGE,"E120.0"),sQuery(id+"F18.wireOp",EDGE,"E120.1"),sQuery(id+"F18.wireOp",EDGE,"E120.2"),sQuery(id+"F18.wireOp",EDGE,"E120.3"),sQuery(id+"F18.wireOp",EDGE,"E120.4"),sQuery(id+"F18.wireOp",EDGE,"E120.5"),sQuery(id+"F18.wireOp",EDGE,"E120.6"),sQuery(id+"F18.wireOp",EDGE,"E120.7")])],"isStart":false});
            var sketch = newSketch(context, id + "F20", { "sketchPlane" : qUnion([Q0])});
            skCircle(sketch, "E121", {"center": v(-105, 27) * mm, "radius": 2.6 * mm});
            skCircle(sketch, "E122", {"center": v(-27, 105) * mm, "radius": 2.6 * mm});
            skCircle(sketch, "E123", {"center": v(26, 105) * mm, "radius": 2.6 * mm});
            skCircle(sketch, "E124", {"center": v(105, -79) * mm, "radius": 2.6 * mm});
            skCircle(sketch, "E125", {"center": v(105, 27) * mm, "radius": 2.6 * mm});
            skCircle(sketch, "E126", {"center": v(-105, -79) * mm, "radius": 2.6 * mm});
            skCircle(sketch, "E127", {"center": v(-105, 80) * mm, "radius": 2.6 * mm});
            skCircle(sketch, "E128", {"center": v(26, -105) * mm, "radius": 2.6 * mm});
            skCircle(sketch, "E129", {"center": v(79, -105) * mm, "radius": 2.6 * mm});
            skCircle(sketch, "E130", {"center": v(-80, -105) * mm, "radius": 2.6 * mm});
            skCircle(sketch, "E131", {"center": v(-27, -105) * mm, "radius": 2.6 * mm});
            skCircle(sketch, "E132", {"center": v(-80, 105) * mm, "radius": 2.6 * mm});
            skCircle(sketch, "E133", {"center": v(105, -26) * mm, "radius": 2.6 * mm});
            skCircle(sketch, "E134", {"center": v(105, 80) * mm, "radius": 2.6 * mm});
            skLineSegment(sketch, "E135", {"start": v(92.5, 117.5) * mm, "end": v(-92.5, 117.5) * mm});
            skArc(sketch, "E136", {"start": v(92.5, 117.5) * mm, "mid": v(110.18, 110.18) * mm, "end": v(117.5, 92.5) * mm});
            skLineSegment(sketch, "E137", {"start": v(117.5, 92.5) * mm, "end": v(117.5, -92.5) * mm});
            skArc(sketch, "E138", {"start": v(117.5, -92.5) * mm, "mid": v(110.18, -110.18) * mm, "end": v(92.5, -117.5) * mm});
            skLineSegment(sketch, "E139", {"start": v(92.5, -117.5) * mm, "end": v(-92.5, -117.5) * mm});
            skArc(sketch, "E140", {"start": v(-92.5, -117.5) * mm, "mid": v(-110.18, -110.18) * mm, "end": v(-117.5, -92.5) * mm});
            skLineSegment(sketch, "E141", {"start": v(-117.5, 92.5) * mm, "end": v(-117.5, -92.5) * mm});
            skArc(sketch, "E142", {"start": v(-117.5, 92.5) * mm, "mid": v(-110.18, 110.18) * mm, "end": v(-92.5, 117.5) * mm});
            skCircle(sketch, "E143", {"center": v(-105, -26) * mm, "radius": 2.6 * mm});
            skArc(sketch, "E144", {"start": v(-91, 75) * mm, "mid": v(-86.31, 86.31) * mm, "end": v(-75, 91) * mm});
            skLineSegment(sketch, "E145", {"start": v(-91, -75) * mm, "end": v(-91, 75) * mm});
            skArc(sketch, "E146", {"start": v(-75, -91) * mm, "mid": v(-86.31, -86.31) * mm, "end": v(-91, -75) * mm});
            skLineSegment(sketch, "E147", {"start": v(75, -91) * mm, "end": v(-75, -91) * mm});
            skArc(sketch, "E148", {"start": v(91, -75) * mm, "mid": v(86.31, -86.31) * mm, "end": v(75, -91) * mm});
            skLineSegment(sketch, "E149", {"start": v(91, 75) * mm, "end": v(91, -75) * mm});
            skArc(sketch, "E150", {"start": v(75, 91) * mm, "mid": v(86.31, 86.31) * mm, "end": v(91, 75) * mm});
            skLineSegment(sketch, "E151", {"start": v(-75, 91) * mm, "end": v(75, 91) * mm});
            skCircle(sketch, "E152", {"center": v(79, 105) * mm, "radius": 2.6 * mm});
            skSolve(sketch);
        }
        {
            var Q0;
            Q0 = qSketchRegion(id + "F20", true);
            extrude(context, id + "F21", {"entities" : qUnion([Q0]), "depth" : 5 * mm});
        }
        {
            var Q0;
            Q0=makeQuery(id+"F21.opExtrude","CAP_FACE",FACE,{"disambiguationData":[OSD([sQuery(id+"F20.wireOp",EDGE,"E121"),sQuery(id+"F20.wireOp",EDGE,"E122"),sQuery(id+"F20.wireOp",EDGE,"E123"),sQuery(id+"F20.wireOp",EDGE,"E124"),sQuery(id+"F20.wireOp",EDGE,"E125"),sQuery(id+"F20.wireOp",EDGE,"E126"),sQuery(id+"F20.wireOp",EDGE,"E127"),sQuery(id+"F20.wireOp",EDGE,"E128"),sQuery(id+"F20.wireOp",EDGE,"E129"),sQuery(id+"F20.wireOp",EDGE,"E130"),sQuery(id+"F20.wireOp",EDGE,"E131"),sQuery(id+"F20.wireOp",EDGE,"E132"),sQuery(id+"F20.wireOp",EDGE,"E133"),sQuery(id+"F20.wireOp",EDGE,"E134"),sQuery(id+"F20.wireOp",EDGE,"E135"),sQuery(id+"F20.wireOp",EDGE,"E136"),sQuery(id+"F20.wireOp",EDGE,"E137"),sQuery(id+"F20.wireOp",EDGE,"E138"),sQuery(id+"F20.wireOp",EDGE,"E139"),sQuery(id+"F20.wireOp",EDGE,"E140"),sQuery(id+"F20.wireOp",EDGE,"E141"),sQuery(id+"F20.wireOp",EDGE,"E142"),sQuery(id+"F20.wireOp",EDGE,"E143"),sQuery(id+"F20.wireOp",EDGE,"E144"),sQuery(id+"F20.wireOp",EDGE,"E145"),sQuery(id+"F20.wireOp",EDGE,"E146"),sQuery(id+"F20.wireOp",EDGE,"E147"),sQuery(id+"F20.wireOp",EDGE,"E148"),sQuery(id+"F20.wireOp",EDGE,"E149"),sQuery(id+"F20.wireOp",EDGE,"E150"),sQuery(id+"F20.wireOp",EDGE,"E151"),sQuery(id+"F20.wireOp",EDGE,"E152")])],"isStart":false});
            var sketch = newSketch(context, id + "F22", { "sketchPlane" : qUnion([Q0])});
            skLineSegment(sketch, "E153", {"start": v(92.5, 117.5) * mm, "end": v(-92.5, 117.5) * mm});
            skArc(sketch, "E154", {"start": v(92.5, 117.5) * mm, "mid": v(110.18, 110.18) * mm, "end": v(117.5, 92.5) * mm});
            skLineSegment(sketch, "E155", {"start": v(117.5, 92.5) * mm, "end": v(117.5, -92.5) * mm});
            skArc(sketch, "E156", {"start": v(117.5, -92.5) * mm, "mid": v(110.18, -110.18) * mm, "end": v(92.5, -117.5) * mm});
            skLineSegment(sketch, "E157", {"start": v(92.5, -117.5) * mm, "end": v(-92.5, -117.5) * mm});
            skArc(sketch, "E158", {"start": v(-92.5, -117.5) * mm, "mid": v(-110.18, -110.18) * mm, "end": v(-117.5, -92.5) * mm});
            skLineSegment(sketch, "E159", {"start": v(-117.5, 92.5) * mm, "end": v(-117.5, -92.5) * mm});
            skArc(sketch, "E160", {"start": v(-117.5, 92.5) * mm, "mid": v(-110.18, 110.18) * mm, "end": v(-92.5, 117.5) * mm});
            skLineSegment(sketch, "E161.bottom", {"start": v(75, 80) * mm, "end": v(-75, 80) * mm});
            skLineSegment(sketch, "E161.top", {"start": v(75, -80) * mm, "end": v(-75, -80) * mm});
            skLineSegment(sketch, "E161.left", {"start": v(80, 75) * mm, "end": v(80, -75) * mm});
            skLineSegment(sketch, "E161.right", {"start": v(-80, 75) * mm, "end": v(-80, -75) * mm});
            skPoint(sketch, "E161.middle", {"position": v(0, 0) * mm});
            skLineSegment(sketch, "E162.bottom", {"start": v(75, 87.5) * mm, "end": v(-75, 87.5) * mm});
            skLineSegment(sketch, "E162.top", {"start": v(75, -87.5) * mm, "end": v(-75, -87.5) * mm});
            skLineSegment(sketch, "E162.left", {"start": v(87.5, 75) * mm, "end": v(87.5, -75) * mm});
            skLineSegment(sketch, "E162.right", {"start": v(-87.5, 75) * mm, "end": v(-87.5, -75) * mm});
            skPoint(sketch, "E163.visualSharp", {"position": v(-80, -80) * mm});
            skArc(sketch, "E163.filletArc", {"start": v(-80, -75) * mm, "mid": v(-78.54, -78.54) * mm, "end": v(-75, -80) * mm});
            skPoint(sketch, "E164.visualSharp", {"position": v(-80, 80) * mm});
            skArc(sketch, "E164.filletArc", {"start": v(-75, 80) * mm, "mid": v(-78.54, 78.54) * mm, "end": v(-80, 75) * mm});
            skPoint(sketch, "E165.visualSharp", {"position": v(80, 80) * mm});
            skArc(sketch, "E165.filletArc", {"start": v(80, 75) * mm, "mid": v(78.54, 78.54) * mm, "end": v(75, 80) * mm});
            skPoint(sketch, "E166.visualSharp", {"position": v(80, -80) * mm});
            skArc(sketch, "E166.filletArc", {"start": v(75, -80) * mm, "mid": v(78.54, -78.54) * mm, "end": v(80, -75) * mm});
            skPoint(sketch, "E167.visualSharp", {"position": v(-87.5, -87.5) * mm});
            skArc(sketch, "E167.filletArc", {"start": v(-87.5, -75) * mm, "mid": v(-83.84, -83.84) * mm, "end": v(-75, -87.5) * mm});
            skPoint(sketch, "E168.visualSharp", {"position": v(-87.5, 87.5) * mm});
            skArc(sketch, "E168.filletArc", {"start": v(-75, 87.5) * mm, "mid": v(-83.84, 83.84) * mm, "end": v(-87.5, 75) * mm});
            skPoint(sketch, "E169.visualSharp", {"position": v(87.5, 87.5) * mm});
            skArc(sketch, "E169.filletArc", {"start": v(87.5, 75) * mm, "mid": v(83.84, 83.84) * mm, "end": v(75, 87.5) * mm});
            skPoint(sketch, "E170.visualSharp", {"position": v(87.5, -87.5) * mm});
            skArc(sketch, "E170.filletArc", {"start": v(75, -87.5) * mm, "mid": v(83.84, -83.84) * mm, "end": v(87.5, -75) * mm});
            skSolve(sketch);
        }
        {
            var Q0;
            Q0 = qSketchRegion(id + "F22", true);
            var Q1;
            Q1=makeQuery(id+"F22.imprint","IMPRINT",FACE,{"disambiguationData":[TD([[makeQuery(id+"F22.imprint","IMPRINT",EDGE,{"derivedFrom":sQuery(id+"F22.wireOp",EDGE,"E161.bottom")}),-1.0]])]});
            extrude(context, id + "F23", {"entities" : qUnion([Q0, Q1]), "depth" : 7.5 * mm});
        }
        {
            var Q0;
            Q0=makeQuery(id+"F23.opExtrude","CAP_FACE",FACE,{"disambiguationData":[OSD([sQuery(id+"F22.wireOp",EDGE,"E153"),sQuery(id+"F22.wireOp",EDGE,"E154"),sQuery(id+"F22.wireOp",EDGE,"E155"),sQuery(id+"F22.wireOp",EDGE,"E156"),sQuery(id+"F22.wireOp",EDGE,"E157"),sQuery(id+"F22.wireOp",EDGE,"E158"),sQuery(id+"F22.wireOp",EDGE,"E159"),sQuery(id+"F22.wireOp",EDGE,"E160"),sQuery(id+"F22.wireOp",EDGE,"E161.bottom"),sQuery(id+"F22.wireOp",EDGE,"E161.top"),sQuery(id+"F22.wireOp",EDGE,"E161.left"),sQuery(id+"F22.wireOp",EDGE,"E161.right"),sQuery(id+"F22.wireOp",EDGE,"E163.filletArc"),sQuery(id+"F22.wireOp",EDGE,"E164.filletArc"),sQuery(id+"F22.wireOp",EDGE,"E165.filletArc"),sQuery(id+"F22.wireOp",EDGE,"E166.filletArc")])],"isStart":true});
            var sketch = newSketch(context, id + "F24", { "sketchPlane" : qUnion([Q0])});
            skLineSegment(sketch, "E171", {"start": v(75, -80) * mm, "end": v(-75, -80) * mm});
            skArc(sketch, "E172", {"start": v(80, -75) * mm, "mid": v(78.54, -78.54) * mm, "end": v(75, -80) * mm});
            skLineSegment(sketch, "E173", {"start": v(80, -75) * mm, "end": v(80, 75) * mm});
            skArc(sketch, "E174", {"start": v(75, 80) * mm, "mid": v(78.54, 78.54) * mm, "end": v(80, 75) * mm});
            skLineSegment(sketch, "E175", {"start": v(75, 80) * mm, "end": v(-75, 80) * mm});
            skArc(sketch, "E176", {"start": v(-80, 75) * mm, "mid": v(-78.54, 78.54) * mm, "end": v(-75, 80) * mm});
            skLineSegment(sketch, "E177", {"start": v(-80, -75) * mm, "end": v(-80, 75) * mm});
            skArc(sketch, "E178", {"start": v(-75, -80) * mm, "mid": v(-78.54, -78.54) * mm, "end": v(-80, -75) * mm});
            skArc(sketch, "E179.0", {"start": v(75, 87.5) * mm, "mid": v(83.84, 83.84) * mm, "end": v(87.5, 75) * mm});
            skLineSegment(sketch, "E179.1", {"start": v(87.5, -75) * mm, "end": v(87.5, 75) * mm});
            skLineSegment(sketch, "E179.2", {"start": v(75, 87.5) * mm, "end": v(-75, 87.5) * mm});
            skArc(sketch, "E179.3", {"start": v(87.5, -75) * mm, "mid": v(83.84, -83.84) * mm, "end": v(75, -87.5) * mm});
            skArc(sketch, "E179.4", {"start": v(-87.5, 75) * mm, "mid": v(-83.84, 83.84) * mm, "end": v(-75, 87.5) * mm});
            skLineSegment(sketch, "E179.5", {"start": v(-87.5, -75) * mm, "end": v(-87.5, 75) * mm});
            skArc(sketch, "E179.6", {"start": v(-75, -87.5) * mm, "mid": v(-83.84, -83.84) * mm, "end": v(-87.5, -75) * mm});
            skLineSegment(sketch, "E179.7", {"start": v(75, -87.5) * mm, "end": v(-75, -87.5) * mm});
            skSolve(sketch);
        }
        {
            var Q0;
            Q0=makeQuery(id+"F24.imprint","IMPRINT",FACE,{"disambiguationData":[TD([[makeQuery(id+"F24.imprint","IMPRINT",EDGE,{"derivedFrom":sQuery(id+"F24.wireOp",EDGE,"E171")}),1.0]])]});
            extrude(context, id + "F25", {"entities" : qUnion([Q0]), "operationType" : NewBodyOperationType.ADD, "depth" : 10 * mm});
        }
        {
            var Q0;
            Q0=makeQuery(id+"F25.opExtrude","CAP_FACE",FACE,{"disambiguationData":[OSD([sQuery(id+"F24.wireOp",EDGE,"E171"),sQuery(id+"F24.wireOp",EDGE,"E172"),sQuery(id+"F24.wireOp",EDGE,"E173"),sQuery(id+"F24.wireOp",EDGE,"E174"),sQuery(id+"F24.wireOp",EDGE,"E175"),sQuery(id+"F24.wireOp",EDGE,"E176"),sQuery(id+"F24.wireOp",EDGE,"E177"),sQuery(id+"F24.wireOp",EDGE,"E178"),sQuery(id+"F24.wireOp",EDGE,"E179.0"),sQuery(id+"F24.wireOp",EDGE,"E179.1"),sQuery(id+"F24.wireOp",EDGE,"E179.2"),sQuery(id+"F24.wireOp",EDGE,"E179.3"),sQuery(id+"F24.wireOp",EDGE,"E179.4"),sQuery(id+"F24.wireOp",EDGE,"E179.5"),sQuery(id+"F24.wireOp",EDGE,"E179.6"),sQuery(id+"F24.wireOp",EDGE,"E179.7")])],"isStart":false});
            fillet(context, id + "F26", {"entities" : qUnion([Q0]), "radius" : 3 * mm, "tangentPropagation" : true, "allowEdgeOverflow" : false});
        }
        {
            var Q0;
            Q0=makeQuery(id+"F23.opExtrude","CAP_FACE",FACE,{"disambiguationData":[OSD([sQuery(id+"F22.wireOp",EDGE,"E153"),sQuery(id+"F22.wireOp",EDGE,"E154"),sQuery(id+"F22.wireOp",EDGE,"E155"),sQuery(id+"F22.wireOp",EDGE,"E156"),sQuery(id+"F22.wireOp",EDGE,"E157"),sQuery(id+"F22.wireOp",EDGE,"E158"),sQuery(id+"F22.wireOp",EDGE,"E159"),sQuery(id+"F22.wireOp",EDGE,"E160"),sQuery(id+"F22.wireOp",EDGE,"E161.bottom"),sQuery(id+"F22.wireOp",EDGE,"E161.top"),sQuery(id+"F22.wireOp",EDGE,"E161.left"),sQuery(id+"F22.wireOp",EDGE,"E161.right"),sQuery(id+"F22.wireOp",EDGE,"E163.filletArc"),sQuery(id+"F22.wireOp",EDGE,"E164.filletArc"),sQuery(id+"F22.wireOp",EDGE,"E165.filletArc"),sQuery(id+"F22.wireOp",EDGE,"E166.filletArc")])],"isStart":false});
            var sketch = newSketch(context, id + "F27", { "sketchPlane" : qUnion([Q0])});
            skLineSegment(sketch, "E180.bottom", {"start": v(105, -105) * mm, "end": v(-105, -105) * mm, "construction": true});
            skLineSegment(sketch, "E180.top", {"start": v(105, 105) * mm, "end": v(-105, 105) * mm, "construction": true});
            skLineSegment(sketch, "E180.left", {"start": v(105, -105) * mm, "end": v(105, 105) * mm, "construction": true});
            skLineSegment(sketch, "E180.right", {"start": v(-105, -105) * mm, "end": v(-105, 105) * mm, "construction": true});
            skPoint(sketch, "E180.middle", {"position": v(0, 0) * mm});
            skLineSegment(sketch, "E181", {"start": v(-105, 0) * mm, "end": v(105, 0) * mm, "construction": true});
            skLineSegment(sketch, "E182", {"start": v(0, 105) * mm, "end": v(0, -105) * mm, "construction": true});
            skLineSegment(sketch, "E183", {"start": v(-105, 53) * mm, "end": v(105, 53) * mm, "construction": true});
            skLineSegment(sketch, "E184", {"start": v(105, -53) * mm, "end": v(-105, -53) * mm, "construction": true});
            skLineSegment(sketch, "E185", {"start": v(-53, 105) * mm, "end": v(-53, -105) * mm, "construction": true});
            skLineSegment(sketch, "E186", {"start": v(53, 105) * mm, "end": v(53, -105) * mm, "construction": true});
            skSolve(sketch);
        }
        {
            var Q0;
            Q0=sQuery(id+"F27.wireOp",VERTEX,"E183.start");
            var Q1;
            Q1=sQuery(id+"F27.wireOp",VERTEX,"E181.start");
            var Q2;
            Q2=sQuery(id+"F27.wireOp",VERTEX,"E184.end");
            var Q3;
            Q3=sQuery(id+"F27.wireOp",VERTEX,"E185.end");
            var Q4;
            Q4=sQuery(id+"F27.wireOp",VERTEX,"E182.end");
            var Q5;
            Q5=sQuery(id+"F27.wireOp",VERTEX,"E186.end");
            var Q6;
            Q6=sQuery(id+"F27.wireOp",VERTEX,"E184.start");
            var Q7;
            Q7=sQuery(id+"F27.wireOp",VERTEX,"E181.end");
            var Q8;
            Q8=sQuery(id+"F27.wireOp",VERTEX,"E183.end");
            var Q9;
            Q9=sQuery(id+"F27.wireOp",VERTEX,"E186.start");
            var Q10;
            Q10=sQuery(id+"F27.wireOp",VERTEX,"E182.start");
            var Q11;
            Q11=sQuery(id+"F27.wireOp",VERTEX,"E185.start");
            var Q12;
            Q12=makeQuery(id+"F23.opExtrude","SWEPT_BODY",BODY,{"disambiguationData":[OSD([sQuery(id+"F22.wireOp",EDGE,"E153"),sQuery(id+"F22.wireOp",EDGE,"E154"),sQuery(id+"F22.wireOp",EDGE,"E155"),sQuery(id+"F22.wireOp",EDGE,"E156"),sQuery(id+"F22.wireOp",EDGE,"E157"),sQuery(id+"F22.wireOp",EDGE,"E158"),sQuery(id+"F22.wireOp",EDGE,"E159"),sQuery(id+"F22.wireOp",EDGE,"E160"),sQuery(id+"F22.wireOp",EDGE,"E161.bottom"),sQuery(id+"F22.wireOp",EDGE,"E161.top"),sQuery(id+"F22.wireOp",EDGE,"E161.left"),sQuery(id+"F22.wireOp",EDGE,"E161.right"),sQuery(id+"F22.wireOp",EDGE,"E163.filletArc"),sQuery(id+"F22.wireOp",EDGE,"E164.filletArc"),sQuery(id+"F22.wireOp",EDGE,"E165.filletArc"),sQuery(id+"F22.wireOp",EDGE,"E166.filletArc")])]});
            var Q13;
            Q13=makeQuery(id+"F21.opExtrude","SWEPT_BODY",BODY,{"disambiguationData":[OSD([sQuery(id+"F20.wireOp",EDGE,"E121"),sQuery(id+"F20.wireOp",EDGE,"E122"),sQuery(id+"F20.wireOp",EDGE,"E123"),sQuery(id+"F20.wireOp",EDGE,"E124"),sQuery(id+"F20.wireOp",EDGE,"E125"),sQuery(id+"F20.wireOp",EDGE,"E126"),sQuery(id+"F20.wireOp",EDGE,"E127"),sQuery(id+"F20.wireOp",EDGE,"E128"),sQuery(id+"F20.wireOp",EDGE,"E129"),sQuery(id+"F20.wireOp",EDGE,"E130"),sQuery(id+"F20.wireOp",EDGE,"E131"),sQuery(id+"F20.wireOp",EDGE,"E132"),sQuery(id+"F20.wireOp",EDGE,"E133"),sQuery(id+"F20.wireOp",EDGE,"E134"),sQuery(id+"F20.wireOp",EDGE,"E135"),sQuery(id+"F20.wireOp",EDGE,"E136"),sQuery(id+"F20.wireOp",EDGE,"E137"),sQuery(id+"F20.wireOp",EDGE,"E138"),sQuery(id+"F20.wireOp",EDGE,"E139"),sQuery(id+"F20.wireOp",EDGE,"E140"),sQuery(id+"F20.wireOp",EDGE,"E141"),sQuery(id+"F20.wireOp",EDGE,"E142"),sQuery(id+"F20.wireOp",EDGE,"E143"),sQuery(id+"F20.wireOp",EDGE,"E144"),sQuery(id+"F20.wireOp",EDGE,"E145"),sQuery(id+"F20.wireOp",EDGE,"E146"),sQuery(id+"F20.wireOp",EDGE,"E147"),sQuery(id+"F20.wireOp",EDGE,"E148"),sQuery(id+"F20.wireOp",EDGE,"E149"),sQuery(id+"F20.wireOp",EDGE,"E150"),sQuery(id+"F20.wireOp",EDGE,"E151"),sQuery(id+"F20.wireOp",EDGE,"E152")])]});
            var Q14;
            Q14=makeQuery(id+"F17.opExtrude","SWEPT_BODY",BODY,{"disambiguationData":[OSD([sQuery(id+"F16.wireOp",EDGE,"E72"),sQuery(id+"F16.wireOp",EDGE,"E73"),sQuery(id+"F16.wireOp",EDGE,"E74"),sQuery(id+"F16.wireOp",EDGE,"E75"),sQuery(id+"F16.wireOp",EDGE,"E76"),sQuery(id+"F16.wireOp",EDGE,"E77"),sQuery(id+"F16.wireOp",EDGE,"E78"),sQuery(id+"F16.wireOp",EDGE,"E79"),sQuery(id+"F16.wireOp",EDGE,"E80"),sQuery(id+"F16.wireOp",EDGE,"E81"),sQuery(id+"F16.wireOp",EDGE,"E82"),sQuery(id+"F16.wireOp",EDGE,"E83"),sQuery(id+"F16.wireOp",EDGE,"E84"),sQuery(id+"F16.wireOp",EDGE,"E85"),sQuery(id+"F16.wireOp",EDGE,"E86"),sQuery(id+"F16.wireOp",EDGE,"E87"),sQuery(id+"F16.wireOp",EDGE,"E88"),sQuery(id+"F16.wireOp",EDGE,"E89"),sQuery(id+"F16.wireOp",EDGE,"E90"),sQuery(id+"F16.wireOp",EDGE,"E91"),sQuery(id+"F16.wireOp",EDGE,"E92"),sQuery(id+"F16.wireOp",EDGE,"E93"),sQuery(id+"F16.wireOp",EDGE,"E94"),sQuery(id+"F16.wireOp",EDGE,"E95")])]});
            var Q15;
            Q15=makeQuery(id+"F4.opExtrude","SWEPT_BODY",BODY,{"disambiguationData":[OSD([sQuery(id+"F0.wireOp",EDGE,"E1.bottom"),sQuery(id+"F0.wireOp",EDGE,"E1.top"),sQuery(id+"F0.wireOp",EDGE,"E1.left"),sQuery(id+"F0.wireOp",EDGE,"E1.right"),sQuery(id+"F0.wireOp",EDGE,"E2.bottom"),sQuery(id+"F0.wireOp",EDGE,"E2.top"),sQuery(id+"F0.wireOp",EDGE,"E2.left"),sQuery(id+"F0.wireOp",EDGE,"E2.right"),sQuery(id+"F0.wireOp",EDGE,"E3.filletArc"),sQuery(id+"F0.wireOp",EDGE,"E4.filletArc"),sQuery(id+"F0.wireOp",EDGE,"E5.filletArc"),sQuery(id+"F0.wireOp",EDGE,"E6.filletArc"),sQuery(id+"F0.wireOp",EDGE,"E11.filletArc"),sQuery(id+"F0.wireOp",EDGE,"E12.filletArc"),sQuery(id+"F0.wireOp",EDGE,"E13.filletArc"),sQuery(id+"F0.wireOp",EDGE,"E14.filletArc")])]});
            var Q16;
            Q16=makeQuery(id+"F15.opExtrude","SWEPT_BODY",BODY,{"disambiguationData":[OSD([sQuery(id+"F14.wireOp",EDGE,"E42"),sQuery(id+"F14.wireOp",EDGE,"E43"),sQuery(id+"F14.wireOp",EDGE,"E44"),sQuery(id+"F14.wireOp",EDGE,"E45"),sQuery(id+"F14.wireOp",EDGE,"E46"),sQuery(id+"F14.wireOp",EDGE,"E47"),sQuery(id+"F14.wireOp",EDGE,"E48"),sQuery(id+"F14.wireOp",EDGE,"E49"),sQuery(id+"F14.wireOp",EDGE,"E50"),sQuery(id+"F14.wireOp",EDGE,"E51"),sQuery(id+"F14.wireOp",EDGE,"E52"),sQuery(id+"F14.wireOp",EDGE,"E53"),sQuery(id+"F14.wireOp",EDGE,"E54"),sQuery(id+"F14.wireOp",EDGE,"E55"),sQuery(id+"F14.wireOp",EDGE,"E56"),sQuery(id+"F14.wireOp",EDGE,"E57"),sQuery(id+"F14.wireOp",EDGE,"E58"),sQuery(id+"F14.wireOp",EDGE,"E59"),sQuery(id+"F14.wireOp",EDGE,"E60"),sQuery(id+"F14.wireOp",EDGE,"E61"),sQuery(id+"F14.wireOp",EDGE,"E37.right"),sQuery(id+"F14.wireOp",EDGE,"E62"),sQuery(id+"F14.wireOp",EDGE,"E37.bottom"),sQuery(id+"F14.wireOp",EDGE,"E63"),sQuery(id+"F14.wireOp",EDGE,"E64"),sQuery(id+"F14.wireOp",EDGE,"E65"),sQuery(id+"F14.wireOp",EDGE,"E66"),sQuery(id+"F14.wireOp",EDGE,"E67"),sQuery(id+"F14.wireOp",EDGE,"E68"),sQuery(id+"F14.wireOp",EDGE,"E69"),sQuery(id+"F14.wireOp",EDGE,"E70"),sQuery(id+"F14.wireOp",EDGE,"E71")])]});
            var Q17;
            Q17=makeQuery(id+"F19.opExtrude","SWEPT_BODY",BODY,{"disambiguationData":[OSD([sQuery(id+"F18.wireOp",EDGE,"E96"),sQuery(id+"F18.wireOp",EDGE,"E97"),sQuery(id+"F18.wireOp",EDGE,"E98"),sQuery(id+"F18.wireOp",EDGE,"E99"),sQuery(id+"F18.wireOp",EDGE,"E100"),sQuery(id+"F18.wireOp",EDGE,"E101"),sQuery(id+"F18.wireOp",EDGE,"E102"),sQuery(id+"F18.wireOp",EDGE,"E103"),sQuery(id+"F18.wireOp",EDGE,"E104"),sQuery(id+"F18.wireOp",EDGE,"E105"),sQuery(id+"F18.wireOp",EDGE,"E106"),sQuery(id+"F18.wireOp",EDGE,"E107"),sQuery(id+"F18.wireOp",EDGE,"E108"),sQuery(id+"F18.wireOp",EDGE,"E109"),sQuery(id+"F18.wireOp",EDGE,"E110"),sQuery(id+"F18.wireOp",EDGE,"E111"),sQuery(id+"F18.wireOp",EDGE,"E112"),sQuery(id+"F18.wireOp",EDGE,"E113"),sQuery(id+"F18.wireOp",EDGE,"E114"),sQuery(id+"F18.wireOp",EDGE,"E115"),sQuery(id+"F18.wireOp",EDGE,"E116"),sQuery(id+"F18.wireOp",EDGE,"E117"),sQuery(id+"F18.wireOp",EDGE,"E118"),sQuery(id+"F18.wireOp",EDGE,"E119"),sQuery(id+"F18.wireOp",EDGE,"E120.0"),sQuery(id+"F18.wireOp",EDGE,"E120.1"),sQuery(id+"F18.wireOp",EDGE,"E120.2"),sQuery(id+"F18.wireOp",EDGE,"E120.3"),sQuery(id+"F18.wireOp",EDGE,"E120.4"),sQuery(id+"F18.wireOp",EDGE,"E120.5"),sQuery(id+"F18.wireOp",EDGE,"E120.6"),sQuery(id+"F18.wireOp",EDGE,"E120.7")])]});
            hole(context, id + "F28", {"style" : HoleStyle.SIMPLE, "endStyle" : HoleEndStyle.THROUGH, "holeDiameter" : 6 * mm, "locations" : qUnion([Q0, Q1, Q2, Q3, Q4, Q5, Q6, Q7, Q8, Q9, Q10, Q11]), "scope" : qUnion([Q12, Q13, Q14, Q15, Q16, Q17]), "isTappedThrough" : true});
        }
    });
